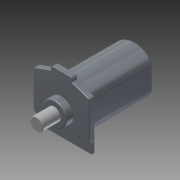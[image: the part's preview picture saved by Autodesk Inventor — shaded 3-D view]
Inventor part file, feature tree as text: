
AUTODESK INVENTOR PART (.ipt)
format: ipt  version: 2014 (Build 180170000, 170)  size: 267,776 bytes
history: native  units: mm
features: fillet x8, extrude x7, sketch x6, chamfer x2
ambient origin geometry x8: Origin, YZ Plane, XZ Plane, XY Plane, X Axis, Y Axis, Z Axis, Center Point
bodies: Solid1 (feature_tree)
feature tree (23):
  extrude  "Extrusion1"  Depth=55.3mm TaperAngle=0.0deg
  sketch  "Sketch2"  dims[d4=53.2mm d5=11.0mm d6=55.3mm d7=0.0mm d8=2.0mm]
  extrude  "Extrusion2"  Depth=2.0mm
  fillet  "Fillet2"  Radius=55.3mm
  fillet  "Fillet1"  Radius=2.0mm
  extrude  "Extrusion3"  Depth=12.9mm
  fillet  "Fillet3"  Radius=6.4mm
  extrude  "Extrusion4"  Depth=2.0mm
  extrude  "Extrusion5"  Depth=1.5mm TaperAngle=0.0deg
  chamfer  "Chamfer1"  Distance=4.5mm
  fillet  "Fillet4"  Radius=2.0mm
  fillet  "Fillet5"  Radius=2.0mm
  fillet  "Fillet6"  Radius=0.5mm
  fillet  "Fillet7"  Radius=45.0mm
  extrude  "Extrusion6"  Depth=2.0mm
  extrude  "Extrusion7"  Depth=2.0mm
  fillet  "Fillet8"  Radius=19.3mm
  chamfer  "Chamfer2"  Distance=5.7mm
  sketch  "Sketch1"  dims[d0=36.0mm d1=55.3mm d2=0.0mm]
  sketch  "Sketch3"  dims[d9=8.0mm d10=12.9mm d11=6.4mm d12=0.0mm]
  sketch  "Sketch4"  dims[d13=0.9mm d15=2.0mm]
  sketch  "Sketch5"  dims[d16=2.0mm d17=1.5mm d18=0.0mm d19=4.5mm d20=0.0mm]
  sketch  "Sketch6"  dims[d21=3.0mm d22=2.0mm d23=45.0deg d24=2.0mm d25=2.0mm d26=0.5mm d28=45.0mm d29=17.0mm d30=2.0mm d31=19.3mm d32=5.7mm d33=0.0mm d34=10.5mm d35=14.3mm d36=0.0mm d37=1.0mm d38=0.5mm d39=2.0mm d40=45.0deg]
